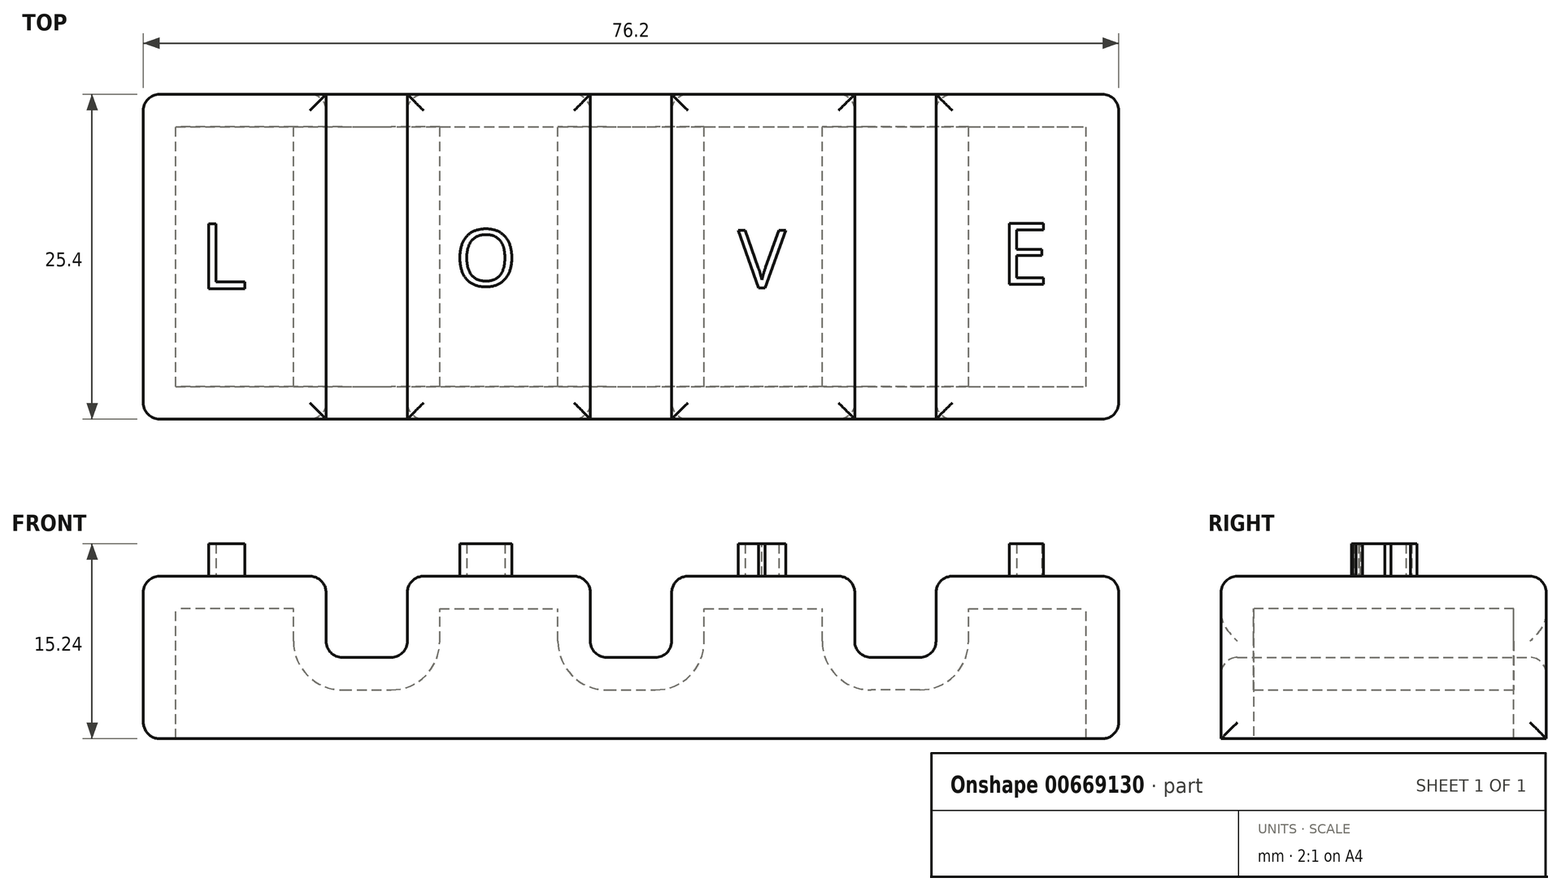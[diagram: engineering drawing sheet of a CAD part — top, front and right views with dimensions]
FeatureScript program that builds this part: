
annotation { "Feature Type Name" : "Feature", "Feature Type Description" : "" }
export const myFeature = defineFeature(function(context is Context, id is Id, definition is map)
    precondition{}
    {
        {
            var Q0;
            Q0=qCreatedBy(makeId("Top.planeOp"),FACE);
            var sketch = newSketch(context, id + "F0", { "sketchPlane" : qUnion([Q0])});
            skLineSegment(sketch, "E0.bottom", {"start": v(-38.1, 12.7) * mm, "end": v(38.1, 12.7) * mm});
            skLineSegment(sketch, "E0.top", {"start": v(-38.1, -12.7) * mm, "end": v(38.1, -12.7) * mm});
            skLineSegment(sketch, "E0.left", {"start": v(-38.1, 12.7) * mm, "end": v(-38.1, -12.7) * mm});
            skLineSegment(sketch, "E0.right", {"start": v(38.1, 12.7) * mm, "end": v(38.1, -12.7) * mm});
            skPoint(sketch, "E0.middle", {"position": v(0, 0) * mm});
            skSolve(sketch);
        }
        {
            var Q0;
            Q0 = qSketchRegion(id + "F0", true);
            extrude(context, id + "F1", {"entities" : qUnion([Q0]), "depth" : 12.7 * mm, "offsetDistance" : 25.4 * mm});
        }
        {
            var Q0;
            Q0=makeQuery(id+"F1.opExtrude","SWEPT_FACE",FACE,{"disambiguationData":[OSD([sQuery(id+"F0.wireOp",EDGE,"E0.bottom")])]});
            var sketch = newSketch(context, id + "F2", { "sketchPlane" : qUnion([Q0])});
            skLineSegment(sketch, "E1", {"start": v(-38.1, 6.35) * mm, "end": v(38.1, 6.35) * mm, "construction": true});
            skLineSegment(sketch, "E2.bottom", {"start": v(-3.18, 6.35) * mm, "end": v(3.17, 6.35) * mm});
            skLineSegment(sketch, "E2.top", {"start": v(-3.18, 19.05) * mm, "end": v(3.17, 19.05) * mm});
            skLineSegment(sketch, "E2.left", {"start": v(-3.18, 6.35) * mm, "end": v(-3.18, 19.05) * mm});
            skLineSegment(sketch, "E2.right", {"start": v(3.17, 6.35) * mm, "end": v(3.17, 19.05) * mm});
            skPoint(sketch, "E2.middle", {"position": v(0, 12.7) * mm});
            skLineSegment(sketch, "E3.bottom", {"start": v(17.48, 6.35) * mm, "end": v(23.83, 6.35) * mm});
            skLineSegment(sketch, "E3.top", {"start": v(17.48, 19.05) * mm, "end": v(23.83, 19.05) * mm});
            skLineSegment(sketch, "E3.left", {"start": v(17.48, 6.35) * mm, "end": v(17.48, 19.05) * mm});
            skLineSegment(sketch, "E3.right", {"start": v(23.83, 6.35) * mm, "end": v(23.83, 19.05) * mm});
            skPoint(sketch, "E3.middle", {"position": v(20.65, 12.7) * mm});
            skLineSegment(sketch, "E4.bottom", {"start": v(-17.48, 6.35) * mm, "end": v(-23.83, 6.35) * mm});
            skLineSegment(sketch, "E4.top", {"start": v(-17.48, 19.05) * mm, "end": v(-23.83, 19.05) * mm});
            skLineSegment(sketch, "E4.left", {"start": v(-17.48, 6.35) * mm, "end": v(-17.48, 19.05) * mm});
            skLineSegment(sketch, "E4.right", {"start": v(-23.83, 6.35) * mm, "end": v(-23.83, 19.05) * mm});
            skPoint(sketch, "E4.middle", {"position": v(-20.65, 12.7) * mm});
            skSolve(sketch);
        }
        {
            var Q0;
            Q0 = qSketchRegion(id + "F2", true);
            extrude(context, id + "F3", {"entities" : qUnion([Q0]), "operationType" : NewBodyOperationType.REMOVE, "endBound" : BoundingType.THROUGH_ALL, "oppositeDirection" : true, "depth" : 25.4 * mm, "offsetDistance" : 25.4 * mm});
        }
        {
            var Q0;
            {var subQ0=sQuery(id+"F0.wireOp",EDGE,"E0.bottom");var subQ1=sQuery(id+"F0.wireOp",EDGE,"E0.right");var subQ2=sQuery(id+"F0.wireOp",EDGE,"E0.top");Q0=makeQuery(id+"F3.boolean.opBoolean","SPLIT",FACE,{"disambiguationData":[TD([makeQuery(id+"F1.opExtrude","SWEPT_FACE",FACE,{"disambiguationData":[OSD([subQ1])]})])],"derivedFrom":makeQuery(id+"F1.opExtrude","CAP_FACE",FACE,{"disambiguationData":[OSD([subQ0,subQ2,sQuery(id+"F0.wireOp",EDGE,"E0.left"),subQ1])],"isStart":false})});}
            var Q1;
            {var subQ0=sQuery(id+"F0.wireOp",EDGE,"E0.bottom");var subQ1=sQuery(id+"F0.wireOp",EDGE,"E0.top");Q1=makeQuery(id+"F3.boolean.opBoolean","SPLIT",FACE,{"disambiguationData":[TD([makeQuery(id+"F3.opExtrude","SWEPT_FACE",FACE,{"disambiguationData":[OSD([sQuery(id+"F2.wireOp",EDGE,"E2.left")])]})])],"derivedFrom":makeQuery(id+"F1.opExtrude","CAP_FACE",FACE,{"disambiguationData":[OSD([subQ0,subQ1,sQuery(id+"F0.wireOp",EDGE,"E0.left"),sQuery(id+"F0.wireOp",EDGE,"E0.right")])],"isStart":false})});}
            fillet(context, id + "F4", {"entities" : qUnion([Q0, Q1]), "radius" : 1.27 * mm, "tangentPropagation" : true, "allowEdgeOverflow" : false});
        }
        {
            var Q0;
            {var subQ0=sQuery(id+"F0.wireOp",EDGE,"E0.bottom");var subQ1=sQuery(id+"F0.wireOp",EDGE,"E0.top");Q0=makeQuery(id+"F3.boolean.opBoolean","SPLIT",FACE,{"disambiguationData":[TD([makeQuery(id+"F3.opExtrude","SWEPT_FACE",FACE,{"disambiguationData":[OSD([sQuery(id+"F2.wireOp",EDGE,"E2.right")])]})])],"derivedFrom":makeQuery(id+"F1.opExtrude","CAP_FACE",FACE,{"disambiguationData":[OSD([subQ0,subQ1,sQuery(id+"F0.wireOp",EDGE,"E0.left"),sQuery(id+"F0.wireOp",EDGE,"E0.right")])],"isStart":false})});}
            var Q1;
            {var subQ0=sQuery(id+"F0.wireOp",EDGE,"E0.bottom");var subQ1=sQuery(id+"F0.wireOp",EDGE,"E0.top");var subQ2=sQuery(id+"F0.wireOp",EDGE,"E0.left");Q1=makeQuery(id+"F3.boolean.opBoolean","SPLIT",FACE,{"disambiguationData":[TD([makeQuery(id+"F1.opExtrude","SWEPT_FACE",FACE,{"disambiguationData":[OSD([subQ2])]})])],"derivedFrom":makeQuery(id+"F1.opExtrude","CAP_FACE",FACE,{"disambiguationData":[OSD([subQ0,subQ1,subQ2,sQuery(id+"F0.wireOp",EDGE,"E0.right")])],"isStart":false})});}
            fillet(context, id + "F5", {"entities" : qUnion([Q0, Q1]), "radius" : 1.27 * mm, "tangentPropagation" : true, "allowEdgeOverflow" : false});
        }
        {
            var Q0;
            Q0=makeQuery(id+"F3.boolean.opBoolean","COPY",FACE,{"derivedFrom":makeQuery(id+"F3.opExtrude","SWEPT_FACE",FACE,{"disambiguationData":[OSD([sQuery(id+"F2.wireOp",EDGE,"E4.bottom")])]})});
            var Q1;
            Q1=makeQuery(id+"F3.boolean.opBoolean","COPY",FACE,{"derivedFrom":makeQuery(id+"F3.opExtrude","SWEPT_FACE",FACE,{"disambiguationData":[OSD([sQuery(id+"F2.wireOp",EDGE,"E2.bottom")])]})});
            var Q2;
            Q2=makeQuery(id+"F3.boolean.opBoolean","COPY",FACE,{"derivedFrom":makeQuery(id+"F3.opExtrude","SWEPT_FACE",FACE,{"disambiguationData":[OSD([sQuery(id+"F2.wireOp",EDGE,"E3.bottom")])]})});
            var Q3;
            Q3=makeQuery(id+"F1.opExtrude","SWEPT_FACE",FACE,{"disambiguationData":[OSD([sQuery(id+"F0.wireOp",EDGE,"E0.right")])]});
            var Q4;
            Q4=makeQuery(id+"F1.opExtrude","SWEPT_FACE",FACE,{"disambiguationData":[OSD([sQuery(id+"F0.wireOp",EDGE,"E0.left")])]});
            fillet(context, id + "F6", {"entities" : qUnion([Q0, Q1, Q2, Q3, Q4]), "radius" : 1.27 * mm, "tangentPropagation" : true, "allowEdgeOverflow" : false});
        }
        {
            var Q0;
            Q0=makeQuery(id+"F1.opExtrude","CAP_FACE",FACE,{"disambiguationData":[OSD([sQuery(id+"F0.wireOp",EDGE,"E0.bottom"),sQuery(id+"F0.wireOp",EDGE,"E0.top"),sQuery(id+"F0.wireOp",EDGE,"E0.left"),sQuery(id+"F0.wireOp",EDGE,"E0.right")])],"isStart":true});
            shell(context, id + "F7", {"entities" : qUnion([Q0]), "thickness" : 2.54 * mm});
        }
        {
            var Q0;
            {var subQ0=sQuery(id+"F0.wireOp",EDGE,"E0.bottom");var subQ1=sQuery(id+"F0.wireOp",EDGE,"E0.top");var subQ2=sQuery(id+"F0.wireOp",EDGE,"E0.left");Q0=makeQuery(id+"F3.boolean.opBoolean","SPLIT",FACE,{"disambiguationData":[TD([makeQuery(id+"F1.opExtrude","SWEPT_FACE",FACE,{"disambiguationData":[OSD([subQ2])]})])],"derivedFrom":makeQuery(id+"F1.opExtrude","CAP_FACE",FACE,{"disambiguationData":[OSD([subQ0,subQ1,subQ2,sQuery(id+"F0.wireOp",EDGE,"E0.right")])],"isStart":false})});}
            var sketch = newSketch(context, id + "F8", { "sketchPlane" : qUnion([Q0])});
            skText(sketch, "E5", { "text": "L", "fontName": "OpenSans-Regular.ttf"});
            skText(sketch, "E6", { "text": "O", "fontName": "OpenSans-Regular.ttf"});
            skText(sketch, "E7", { "text": "V", "fontName": "OpenSans-Regular.ttf"});
            skText(sketch, "E8", { "text": "E", "fontName": "OpenSans-Regular.ttf"});
            const initialGuessF8  = {"E5": [-0.0337, -0.0025, 1, 0, 0.00512], "E6": [-0.01375, -0.0023, 1, 0, 0.00445], "E7": [0.00836, -0.00243, 1, 0, 0.00452], "E8": [0.02891, -0.00216, 1, 0, 0.00479]};
            skSetInitialGuess(sketch, initialGuessF8);
            skSolve(sketch);
        }
        {
            var Q0;
            Q0 = qSketchRegion(id + "F8", true);
            extrude(context, id + "F9", {"entities" : qUnion([Q0]), "operationType" : NewBodyOperationType.ADD, "depth" : 2.54 * mm, "offsetDistance" : 25.4 * mm});
        }
    });
